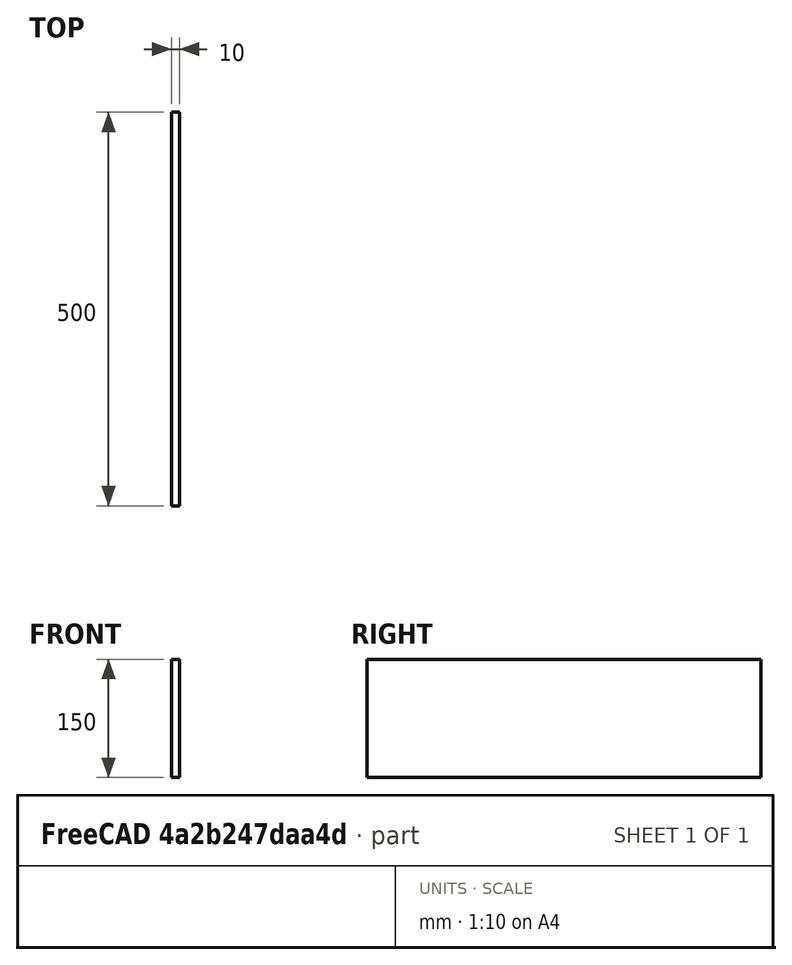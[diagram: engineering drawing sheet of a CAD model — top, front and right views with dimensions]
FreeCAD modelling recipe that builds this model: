
FCSTD DOCUMENT  (FreeCAD 0.18R16131 (Git))
Label: 4000_Body_Back_02_YZ
License: All rights reserved
LicenseURL: http://en.wikipedia.org/wiki/All_rights_reserved
objects: Sketcher::SketchObject×1, Spreadsheet::Sheet×1, PartDesign::Pad×1, PartDesign::Body×1
note: 4 computed .brp shape members not serialized (recipe doc carries the construction recipe); baked Part::Feature solids carry a one-line shape summary decoded from their .brp

FEATURE [Sketcher::SketchObject] Sketch
  MapMode = 4
  Placement = pos=(0,0,0) rot=(0.57735,0.57735,0.57735;2.0944rad)
  Support = -> [XY_Plane]
  expr: Constraints[6] = Spreadsheet.nY
  expr: Constraints[5] = Spreadsheet.nZ
  sketch-geometry (5):
    g0: LineSegment StartX=0 StartY=0 StartZ=0 EndX=0 EndY=150 EndZ=0
    g1: LineSegment StartX=500 StartY=0 StartZ=0 EndX=500 EndY=150 EndZ=0
    g2: LineSegment StartX=500 StartY=150 StartZ=0 EndX=0 EndY=150 EndZ=0
    g3: LineSegment StartX=250 StartY=0 StartZ=0 EndX=0 EndY=0 EndZ=0
    g4: LineSegment StartX=500 StartY=0 StartZ=0 EndX=250 EndY=0 EndZ=0
  constraints (14):
    c: Vertical(g0)
    c: Vertical(g1)
    c: Coincident(g2,g1)
    c: Coincident(g2,g0)
    c: Horizontal(g2)
    c: DistanceY(g1,g1) = 150
    c: DistanceX(g2,g2) = 500
    c: Coincident(g3,g0)
    c: Coincident(g4,g1)
    c: Horizontal(g4)
    c: Equal(g3,g4)
    c: Coincident(g4,g3)
    c: Horizontal(g3)
    c: Coincident(g0,g-1)
FEATURE [Spreadsheet::Sheet] Spreadsheet  label="xls"
  cells = B7=KEYBOARD FRONT; B8=Width; C8=nY; D8(nY)=500; B9=Height; C9=nZ; D9(nZ)=150; E9=F(T); B10=Thickness; C10=nT; D10(nT)=10
FEATURE [PartDesign::Pad] Pad
  Length = 10
  Length2 = 100
  Profile = -> Sketch
  Reversed = true
  Type = 0
  expr: Length = Spreadsheet.nT
FEATURE [PartDesign::Body] Body
  Group = -> [Sketch,Pad]
  Origin = -> Origin
  Tip = -> Pad
